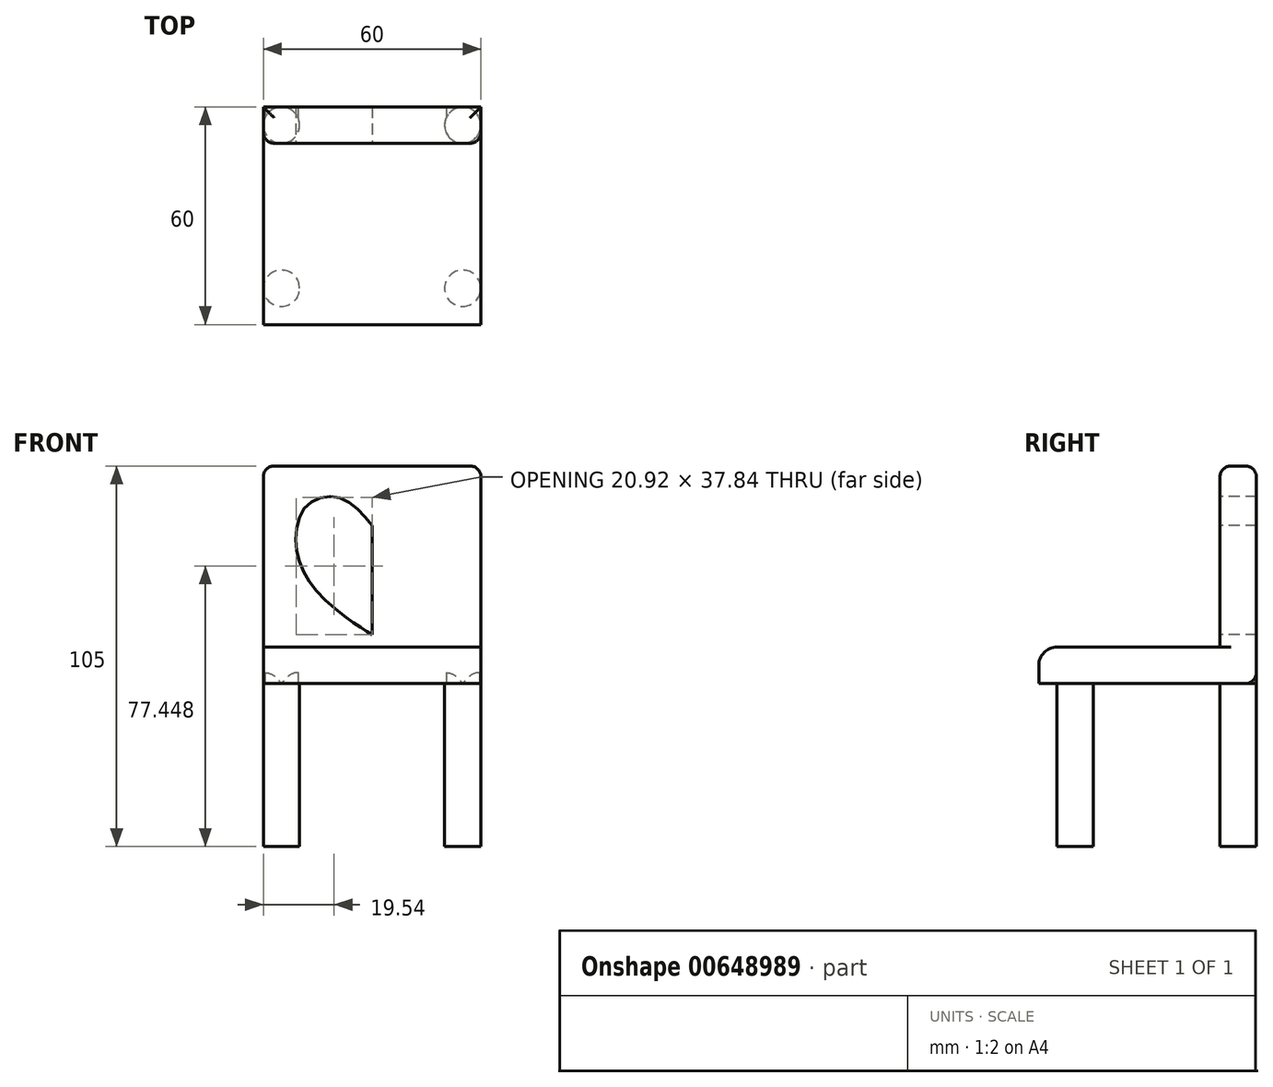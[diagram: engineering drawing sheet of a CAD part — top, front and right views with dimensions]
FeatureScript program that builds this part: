
annotation { "Feature Type Name" : "Feature", "Feature Type Description" : "" }
export const myFeature = defineFeature(function(context is Context, id is Id, definition is map)
    precondition{}
    {
        {
            var Q0;
            Q0=qCreatedBy(makeId("Top.planeOp"),FACE);
            var sketch = newSketch(context, id + "F0", { "sketchPlane" : qUnion([Q0])});
            skLineSegment(sketch, "E0.bottom", {"start": v(-30, 30) * mm, "end": v(30, 30) * mm});
            skLineSegment(sketch, "E0.top", {"start": v(-30, -30) * mm, "end": v(30, -30) * mm});
            skLineSegment(sketch, "E0.left", {"start": v(-30, 30) * mm, "end": v(-30, -30) * mm});
            skLineSegment(sketch, "E0.right", {"start": v(30, 30) * mm, "end": v(30, -30) * mm});
            skPoint(sketch, "E0.middle", {"position": v(0, 0) * mm});
            skSolve(sketch);
        }
        {
            var Q0;
            Q0 = qSketchRegion(id + "F0", true);
            extrude(context, id + "F1", {"entities" : qUnion([Q0]), "depth" : 10 * mm, "offsetDistance" : 25 * mm});
        }
        {
            var Q0;
            Q0=makeQuery(id+"F1.opExtrude","CAP_FACE",FACE,{"disambiguationData":[OSD([sQuery(id+"F0.wireOp",EDGE,"E0.bottom"),sQuery(id+"F0.wireOp",EDGE,"E0.top"),sQuery(id+"F0.wireOp",EDGE,"E0.left"),sQuery(id+"F0.wireOp",EDGE,"E0.right")])],"isStart":true});
            var sketch = newSketch(context, id + "F2", { "sketchPlane" : qUnion([Q0])});
            skCircle(sketch, "E1", {"center": v(25, -25) * mm, "radius": 5 * mm});
            skSolve(sketch);
        }
        {
            var Q0;
            Q0 = qSketchRegion(id + "F2", true);
            extrude(context, id + "F3", {"entities" : qUnion([Q0]), "operationType" : NewBodyOperationType.ADD, "depth" : 45 * mm, "offsetDistance" : 25 * mm});
        }
        {
            var Q0;
            Q0=makeQuery(id+"F1.opExtrude","SWEPT_BODY",BODY,{"disambiguationData":[OSD([sQuery(id+"F0.wireOp",EDGE,"E0.bottom"),sQuery(id+"F0.wireOp",EDGE,"E0.top"),sQuery(id+"F0.wireOp",EDGE,"E0.left"),sQuery(id+"F0.wireOp",EDGE,"E0.right")])]});
            var Q1;
            Q1=qCreatedBy(makeId("Right.planeOp"),FACE);
            mirror(context, id + "F4", {"operationType" : NewBodyOperationType.ADD, "entities" : qUnion([Q0]), "mirrorPlane" : qUnion([Q1])});
        }
        {
            var Q0;
            {var subQ0=sQuery(id+"F0.wireOp",EDGE,"E0.left");var subQ1=makeQuery(id+"F1.opExtrude","SWEPT_FACE",FACE,{"disambiguationData":[OSD([subQ0])]});var subQ2=sQuery(id+"F0.wireOp",EDGE,"E0.top");var subQ3=makeQuery(id+"F1.opExtrude","SWEPT_FACE",FACE,{"disambiguationData":[OSD([subQ2])]});var subQ4=makeQuery(id+"F3.opExtrude","SWEPT_FACE",FACE,{"disambiguationData":[OSD([sQuery(id+"F2.wireOp",EDGE,"E1")])]});var subQ5=sQuery(id+"F0.wireOp",EDGE,"E0.right");var subQ6=sQuery(id+"F0.wireOp",EDGE,"E0.bottom");var subQ7=makeQuery(id+"F1.opExtrude","CAP_FACE",FACE,{"disambiguationData":[OSD([subQ6,subQ2,subQ0,subQ5])],"isStart":true});var subQ8=makeQuery(id+"F1.opExtrude","SWEPT_FACE",FACE,{"disambiguationData":[OSD([subQ6])]});var subQ9=makeQuery(id+"F1.opExtrude","SWEPT_FACE",FACE,{"disambiguationData":[OSD([subQ5])]});Q0=makeQuery(id+"F4.boolean.opBoolean","SPLIT",FACE,{"disambiguationData":[TD([subQ8,subQ7,subQ3,subQ1,subQ9,subQ4,makeQuery(id+"F4.opPattern","COPY",FACE,{"derivedFrom":subQ4,"instanceName":"1"})])],"derivedFrom":makeQuery(id+"F3.boolean.opBoolean","SPLIT",FACE,{"disambiguationData":[TD([subQ8,subQ7,subQ3,subQ1,subQ9,subQ4])],"derivedFrom":subQ7})});}
            var sketch = newSketch(context, id + "F5", { "sketchPlane" : qUnion([Q0])});
            skCircle(sketch, "E2", {"center": v(-25, 20) * mm, "radius": 5 * mm});
            skSolve(sketch);
        }
        {
            var Q0;
            Q0 = qSketchRegion(id + "F5", true);
            extrude(context, id + "F6", {"entities" : qUnion([Q0]), "operationType" : NewBodyOperationType.ADD, "depth" : 45 * mm, "offsetDistance" : 25 * mm});
        }
        {
            var Q0;
            Q0=makeQuery(id+"F1.opExtrude","SWEPT_BODY",BODY,{"disambiguationData":[OSD([sQuery(id+"F0.wireOp",EDGE,"E0.bottom"),sQuery(id+"F0.wireOp",EDGE,"E0.top"),sQuery(id+"F0.wireOp",EDGE,"E0.left"),sQuery(id+"F0.wireOp",EDGE,"E0.right")])]});
            var Q1;
            Q1=qCreatedBy(makeId("Right.planeOp"),FACE);
            mirror(context, id + "F7", {"operationType" : NewBodyOperationType.ADD, "entities" : qUnion([Q0]), "mirrorPlane" : qUnion([Q1])});
        }
        {
            var Q0;
            Q0=makeQuery(id+"F1.opExtrude","CAP_EDGE",EDGE,{"disambiguationData":[OSD([sQuery(id+"F0.wireOp",EDGE,"E0.top")])],"isStart":false});
            fillet(context, id + "F8", {"entities" : qUnion([Q0]), "radius" : 5 * mm, "tangentPropagation" : true, "allowEdgeOverflow" : false});
        }
        {
            var Q0;
            Q0=makeQuery(id+"F1.opExtrude","CAP_FACE",FACE,{"disambiguationData":[OSD([sQuery(id+"F0.wireOp",EDGE,"E0.bottom"),sQuery(id+"F0.wireOp",EDGE,"E0.top"),sQuery(id+"F0.wireOp",EDGE,"E0.left"),sQuery(id+"F0.wireOp",EDGE,"E0.right")])],"isStart":false});
            var sketch = newSketch(context, id + "F9", { "sketchPlane" : qUnion([Q0])});
            skLineSegment(sketch, "E3", {"start": v(0, 20) * mm, "end": v(0, 25) * mm});
            skLineSegment(sketch, "E4.bottom", {"start": v(-30, 30) * mm, "end": v(30, 30) * mm});
            skLineSegment(sketch, "E4.top", {"start": v(-30, 20) * mm, "end": v(30, 20) * mm});
            skLineSegment(sketch, "E4.left", {"start": v(-30, 30) * mm, "end": v(-30, 20) * mm});
            skLineSegment(sketch, "E4.right", {"start": v(30, 30) * mm, "end": v(30, 20) * mm});
            skPoint(sketch, "E4.middle", {"position": v(0, 25) * mm});
            skSolve(sketch);
        }
        {
            var Q0;
            Q0 = qSketchRegion(id + "F9", true);
            extrude(context, id + "F10", {"entities" : qUnion([Q0]), "operationType" : NewBodyOperationType.ADD, "depth" : 50 * mm, "offsetDistance" : 25 * mm});
        }
        {
            var Q0;
            Q0=makeQuery(id+"F10.opExtrude","CAP_FACE",FACE,{"disambiguationData":[OSD([sQuery(id+"F9.wireOp",EDGE,"E4.bottom"),sQuery(id+"F9.wireOp",EDGE,"E4.top"),sQuery(id+"F9.wireOp",EDGE,"E4.left"),sQuery(id+"F9.wireOp",EDGE,"E4.right")])],"isStart":false});
            var Q1;
            {var subQ0=sQuery(id+"F0.wireOp",EDGE,"E0.bottom");var subQ2=makeQuery(id+"F3.opExtrude","SWEPT_FACE",FACE,{"disambiguationData":[OSD([sQuery(id+"F2.wireOp",EDGE,"E1")])]});var subQ3=sQuery(id+"F0.wireOp",EDGE,"E0.left");Q1=makeQuery(id+"F4.boolean.opBoolean","SPLIT",EDGE,{"disambiguationData":[TD([subQ2])],"derivedFrom":makeQuery(id+"F3.boolean.opBoolean","SPLIT",EDGE,{"disambiguationData":[TD([makeQuery(id+"F1.opExtrude","SWEPT_FACE",FACE,{"disambiguationData":[OSD([subQ3])]})])],"derivedFrom":makeQuery(id+"F1.opExtrude","CAP_EDGE",EDGE,{"disambiguationData":[OSD([subQ0])],"isStart":true})})});}
            var Q2;
            Q2=makeQuery(id+"F10.opExtrude","SWEPT_EDGE",EDGE,{"disambiguationData":[OSD([sQuery(id+"F0.wireOp",EDGE,"E0.left"),sQuery(id+"F9.wireOp",EDGE,"E4.top"),sQuery(id+"F9.wireOp",EDGE,"E4.left")])]});
            var Q3;
            Q3=makeQuery(id+"F10.opExtrude","SWEPT_EDGE",EDGE,{"disambiguationData":[OSD([sQuery(id+"F0.wireOp",EDGE,"E0.right"),sQuery(id+"F9.wireOp",EDGE,"E4.top"),sQuery(id+"F9.wireOp",EDGE,"E4.right")])]});
            fillet(context, id + "F11", {"entities" : qUnion([Q0, Q1, Q2, Q3]), "radius" : 3 * mm, "tangentPropagation" : true, "allowEdgeOverflow" : false});
        }
        {
            var Q0;
            Q0=makeQuery(id+"F10.opExtrude","SWEPT_FACE",FACE,{"disambiguationData":[OSD([sQuery(id+"F9.wireOp",EDGE,"E4.top")])]});
            var sketch = newSketch(context, id + "F12", { "sketchPlane" : qUnion([Q0])});
            skFitSpline(sketch, "E5", {"points": [v(0, 43.53) * mm, v(-8.8, 51.14) * mm, v(-18.07, 49.04) * mm, v(-20.9, 37.96) * mm, v(-15.96, 26.23) * mm, v(-4.62, 16.4) * mm, v(0, 13.53) * mm], "startDerivative": vector(-45.9, 56.26) * mm, "endDerivative": vector(33.83, -19.6) * mm});
            skFitSpline(sketch, "E6", {"points": [v(0, 13.53) * mm, v(0, 43.53) * mm], "startDerivative": vector(0, 30) * mm, "endDerivative": vector(0, 30) * mm});
            skSolve(sketch);
        }
        {
            var Q0;
            Q0 = qSketchRegion(id + "F12", true);
            extrude(context, id + "F13", {"entities" : qUnion([Q0]), "operationType" : NewBodyOperationType.REMOVE, "oppositeDirection" : true, "depth" : 10 * mm, "offsetDistance" : 25 * mm});
        }
    });
